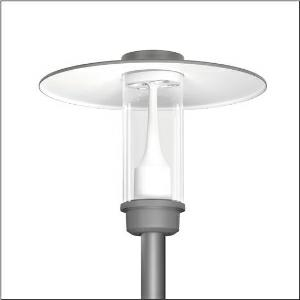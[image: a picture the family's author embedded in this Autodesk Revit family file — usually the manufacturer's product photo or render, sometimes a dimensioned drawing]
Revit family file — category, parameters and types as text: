
# Revit family: litepole_2_iq___pl1_2s_5xa5425rf14h_b6f1
name_source: partatom
category: Lighting Fixtures
units: mm (PartAtom-declared; Revit-internal decimal feet)

## family parameters
Cut with Voids When Loaded = No
Host = Face
Light Source = No
Part Type = Normal
Room Calculation Point = No
Round Connector Dimension = Use Diameter
Shared = No

## types (1)
- --- (1 x LED, 2990 lm, 18.5 W, 4000K)
    Apparent Load = 19 VA
    CIE Flux Codes = 22 60 92 98 100
    Color Rendering = 70
    Color Temperature = 4000K
    Default Elevation = 1800 mm
    Description = Litepole 2 iQ, mast luminaire, Module 540 iQ-SR, primary light control with 3 zone facetted reflector, of plastic, silver coated, highly specular, structured, primary optical cover: cover, of PMMA, transparent, light distribution: PL1.2s, light emission: direct distribution, primary light characteristic: symmetric, installation type: post-top, LED, High Power LED, rated luminous flux: 2.990lm, luminous efficacy: 162lm/W, light colour: 740, colour temperature: 4000K, control gear: iQ Street-Remote, control: pre-setting: logarithmic dimming characteristic, Street-Remote, Auto-Match, Temp-Guard, Lumen-Switch, Night-Set, Smart-Wire, Light-Fading, Desk-Remote (wireless, voltage-free reading and setting of iQ features in the workshop via application-optimized NFC function/RFID function), optimised constant luminous flux control (CLO 2.0), with terminal, 6-pole, max. 2.5mm², mains connection: 230..240V, AC, 50/60Hz, start of lifetime: 19W, end of service life: 20W, reduction: 10W, luminaire housing, upper part, of aluminium, coated, Siteco® metallic grey (DB 702S), diameter: 750mm, height: 590mm, spigot size: d x l = 76 x 70mm (post-top) | with reducer (optional accessory) 60 x 70mm, mounting height: 3..5m, post-top mast mounting element, of diecast aluminium, coated, Siteco® metallic grey (DB 702S), Module 540 iQ-SR, traffic white (RAL 9016), equipment: standard, protection rating (complete): IP65, insulation class (complete): insulation class II (safety insulation), certification: CE, ENEC, VDE, packaging unit: 1 piece

Light Distribution: PL1.2s
    Height = 590 mm
    Lamp = 1 x LED
    Lamp Light Flux = 2990 lm
    Lamp Power = 18.5 W
    Lamp count = 1
    Length = 750 mm
    Luminous efficacy = 162 lm/W
    Manufacturer = Siteco
    ModVariant = No
    Model = 5XA5425RF14H
    Number of Poles = 1
    OnlyDefault = Yes
    Power Factor = 1
    Product Name = Litepole 2 iQ | PL1.2s
    Product group = mast luminaire | pylon top
    ProductGroupID = 6100
    Protection Class = Protection class II
    Protection Degree = IP 65
    RLX_Detail_Level = 1
    RLX_Emergency_Light_Flux = 0 lm
    RLX_Emergency_Type = 0
    RLX_Emergency_Type_DB = No
    RlxData = <blob elided: 29461 chars, md5=91d05767>
    Socket = socket
    Standby Power = 0 W
    System Light Flux = 2990 lm
    System Power = 19 W
    Type Comments = factory setting: luminous flux: 100 % | dim-lin: 254 | 385 mA
    Type Image = l_1006518.jpg
    URL = http://relux.com
    VarID = @adj_144105
    Voltage = 0 V
    Weight = 0.00 kg
    Width = 0 mm  [stored 0 ft]

note: [stored X ft] marks values corroborated as IEEE doubles in the binary element streams (Revit-internal decimal feet)

## geometry (parser evidence)
native form markers: Blend x4, Sweep x9
no freeform markers — native parametric forms only
